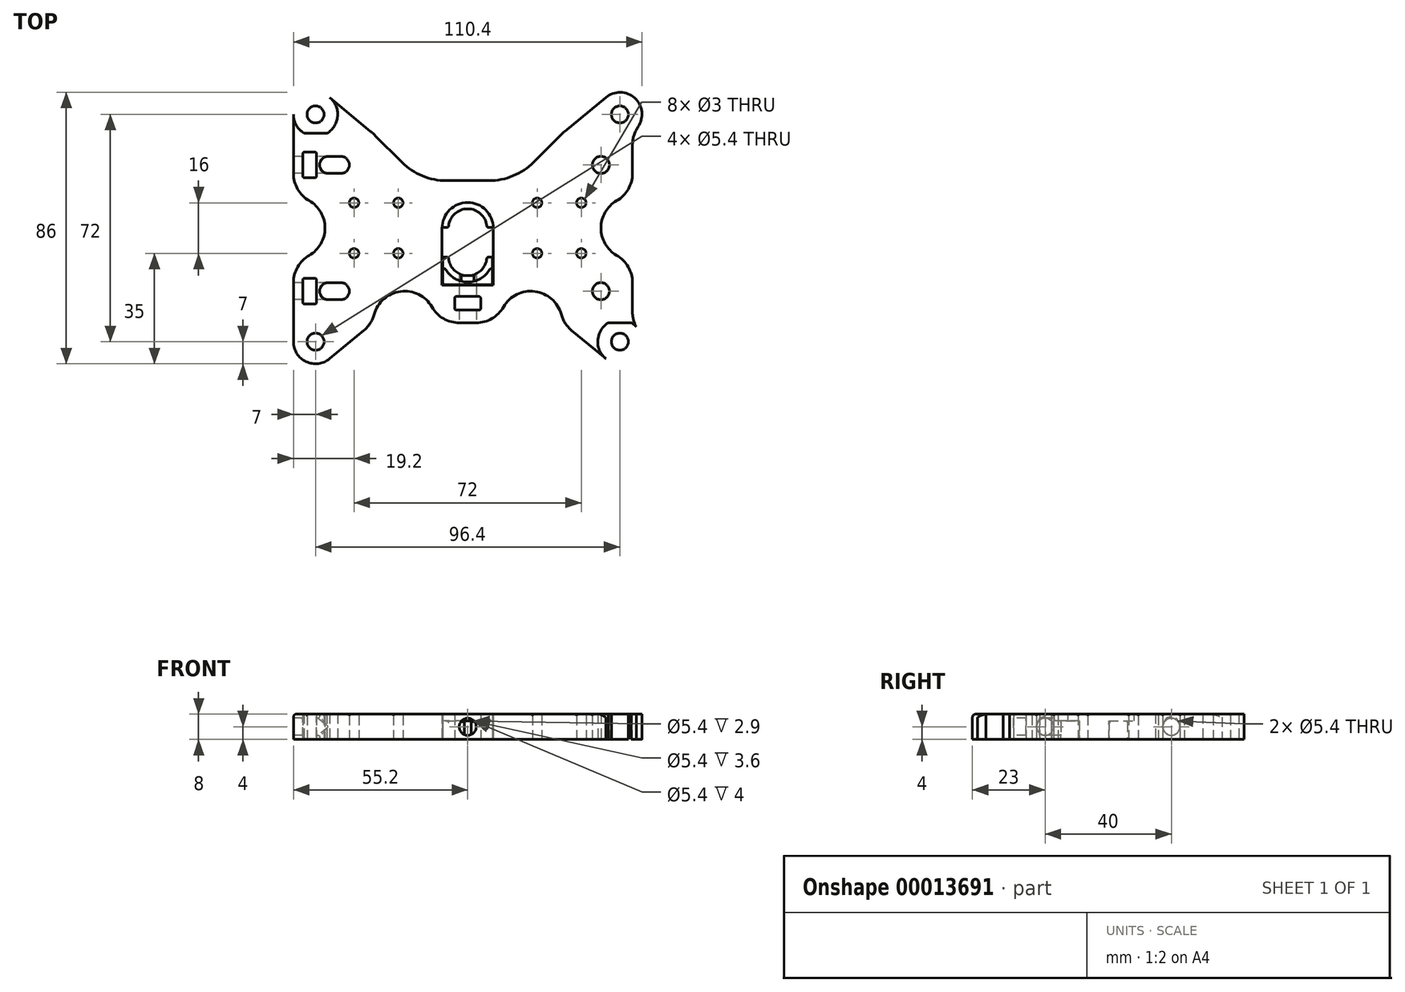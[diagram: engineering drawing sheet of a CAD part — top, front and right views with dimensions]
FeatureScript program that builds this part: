
annotation { "Feature Type Name" : "Feature", "Feature Type Description" : "" }
export const myFeature = defineFeature(function(context is Context, id is Id, definition is map)
    precondition{}
    {
        {
            var Q0;
            Q0=qCreatedBy(makeId("Top.planeOp"),FACE);
            var sketch = newSketch(context, id + "F0", { "sketchPlane" : qUnion([Q0])});
            skLineSegment(sketch, "E0", {"start": v(-12, 175) * mm, "end": v(-12, -175) * mm, "construction": true});
            skLineSegment(sketch, "E1", {"start": v(-32, 175) * mm, "end": v(-32, -175) * mm, "construction": true});
            skLineSegment(sketch, "E2", {"start": v(-32, -175) * mm, "end": v(-12, -175) * mm, "construction": true});
            skLineSegment(sketch, "E3", {"start": v(-32, 175) * mm, "end": v(-12, 175) * mm, "construction": true});
            skLineSegment(sketch, "E4", {"start": v(-12, 0) * mm, "end": v(0, 0) * mm, "construction": true});
            skLineSegment(sketch, "E5", {"start": v(0, 0) * mm, "end": v(0, 158.46) * mm, "construction": true});
            skLineSegment(sketch, "E6.0.MirrorCS", {"start": v(12, 175) * mm, "end": v(12, -175) * mm, "construction": true});
            skLineSegment(sketch, "E7.0.MirrorCS", {"start": v(32, 175) * mm, "end": v(12, 175) * mm, "construction": true});
            skLineSegment(sketch, "E8.0.MirrorCS", {"start": v(32, 175) * mm, "end": v(32, -175) * mm, "construction": true});
            skLineSegment(sketch, "E9.0.MirrorCS", {"start": v(32, -175) * mm, "end": v(12, -175) * mm, "construction": true});
            skLineSegment(sketch, "E10.rect.bottom", {"start": v(42.2, 20) * mm, "end": v(-42.2, 20) * mm, "construction": true});
            skLineSegment(sketch, "E10.rect.top", {"start": v(42.2, -20) * mm, "end": v(-42.2, -20) * mm, "construction": true});
            skLineSegment(sketch, "E10.rect.left", {"start": v(42.2, 20) * mm, "end": v(42.2, -20) * mm, "construction": true});
            skLineSegment(sketch, "E10.rect.right", {"start": v(-42.2, 20) * mm, "end": v(-42.2, -20) * mm, "construction": true});
            skPoint(sketch, "E10.rect.middle", {"position": v(0, 0) * mm});
            skCircle(sketch, "E11", {"center": v(-42.2, 20) * mm, "radius": 12 * mm, "construction": true});
            skCircle(sketch, "E12", {"center": v(42.2, 20) * mm, "radius": 12 * mm, "construction": true});
            skCircle(sketch, "E13", {"center": v(42.2, -20) * mm, "radius": 12 * mm, "construction": true});
            skCircle(sketch, "E14", {"center": v(-42.2, -20) * mm, "radius": 12 * mm, "construction": true});
            skLineSegment(sketch, "E15", {"start": v(-30.2, 175) * mm, "end": v(-30.2, -175) * mm, "construction": true});
            skLineSegment(sketch, "E16", {"start": v(30.2, -175) * mm, "end": v(30.2, 175) * mm, "construction": true});
            skLineSegment(sketch, "E17", {"start": v(-30.2, 0) * mm, "end": v(-32, 0) * mm, "construction": true});
            skLineSegment(sketch, "E18", {"start": v(32, 0) * mm, "end": v(30.2, 0) * mm, "construction": true});
            skArc(sketch, "E19", {"start": v(8.1, 0) * mm, "mid": v(0, 8.1) * mm, "end": v(-8.1, 0) * mm});
            skLineSegment(sketch, "E20.rect.bottom", {"start": v(52.2, 30) * mm, "end": v(-55.2, 30) * mm});
            skLineSegment(sketch, "E20.rect.top", {"start": v(52.2, -30) * mm, "end": v(-55.2, -30) * mm});
            skLineSegment(sketch, "E20.rect.left", {"start": v(52.2, 30) * mm, "end": v(52.2, -30) * mm});
            skLineSegment(sketch, "E20.rect.right", {"start": v(-55.2, 30) * mm, "end": v(-55.2, -30) * mm});
            skCircle(sketch, "E21", {"center": v(42.2, 20) * mm, "radius": 2.7 * mm});
            skCircle(sketch, "E22", {"center": v(42.2, -20) * mm, "radius": 2.7 * mm});
            skArc(sketch, "E23", {"start": v(6.1, 0.2) * mm, "mid": v(0, 6.1) * mm, "end": v(-6.1, 0.2) * mm});
            skCircle(sketch, "E24", {"center": v(0, -6) * mm, "radius": 8.1 * mm, "construction": true});
            skLineSegment(sketch, "E25", {"start": v(-8.1, -9.2) * mm, "end": v(-8.1, -18.1) * mm});
            skLineSegment(sketch, "E26", {"start": v(8.1, -9.2) * mm, "end": v(8.1, -18.1) * mm});
            skLineSegment(sketch, "E27", {"start": v(-8.1, -18.1) * mm, "end": v(8.1, -18.1) * mm});
            skArc(sketch, "E28", {"start": v(-6.1, -9) * mm, "mid": v(0, -15.1) * mm, "end": v(6.1, -9) * mm});
            skLineSegment(sketch, "E29.rect.bottom", {"start": v(4.1, -26) * mm, "end": v(-4.1, -26) * mm});
            skLineSegment(sketch, "E29.rect.top", {"start": v(4.1, -21.7) * mm, "end": v(-4.1, -21.7) * mm});
            skLineSegment(sketch, "E29.rect.left", {"start": v(4.1, -26) * mm, "end": v(4.1, -21.7) * mm});
            skLineSegment(sketch, "E29.rect.right", {"start": v(-4.1, -26) * mm, "end": v(-4.1, -21.7) * mm});
            skPoint(sketch, "E29.rect.middle", {"position": v(0, -23.85) * mm});
            skLineSegment(sketch, "E30", {"start": v(6.1, 0.2) * mm, "end": v(8.1, 0.2) * mm});
            skLineSegment(sketch, "E31", {"start": v(-6.1, 0.2) * mm, "end": v(-8.1, 0.2) * mm});
            skLineSegment(sketch, "E32", {"start": v(6.1, -9.2) * mm, "end": v(8.1, -9.2) * mm});
            skLineSegment(sketch, "E33", {"start": v(-6.1, -9.2) * mm, "end": v(-8.1, -9.2) * mm});
            skLineSegment(sketch, "E34.rect.bottom", {"start": v(-47.9, 24.1) * mm, "end": v(-52.2, 24.1) * mm});
            skLineSegment(sketch, "E34.rect.top", {"start": v(-47.9, 15.9) * mm, "end": v(-52.2, 15.9) * mm});
            skLineSegment(sketch, "E34.rect.left", {"start": v(-47.9, 24.1) * mm, "end": v(-47.9, 15.9) * mm});
            skLineSegment(sketch, "E34.rect.right", {"start": v(-52.2, 24.1) * mm, "end": v(-52.2, 15.9) * mm});
            skPoint(sketch, "E34.rect.middle", {"position": v(-50.05, 20) * mm});
            skLineSegment(sketch, "E35.0.MirrorCS", {"start": v(-47.9, -15.9) * mm, "end": v(-52.2, -15.9) * mm});
            skLineSegment(sketch, "E36.0.MirrorCS", {"start": v(-47.9, -24.1) * mm, "end": v(-47.9, -15.9) * mm});
            skLineSegment(sketch, "E37.0.MirrorCS", {"start": v(-47.9, -24.1) * mm, "end": v(-52.2, -24.1) * mm});
            skLineSegment(sketch, "E38.0.MirrorCS", {"start": v(-52.2, -24.1) * mm, "end": v(-52.2, -15.9) * mm});
            skArc(sketch, "E39", {"start": v(-44.2, 22.7) * mm, "mid": v(-46.9, 20) * mm, "end": v(-44.2, 17.3) * mm});
            skArc(sketch, "E40", {"start": v(-40.2, 17.3) * mm, "mid": v(-37.5, 20) * mm, "end": v(-40.2, 22.7) * mm});
            skLineSegment(sketch, "E41", {"start": v(-40.2, 17.3) * mm, "end": v(-44.2, 17.3) * mm});
            skLineSegment(sketch, "E42", {"start": v(-44.2, 22.7) * mm, "end": v(-40.2, 22.7) * mm});
            skArc(sketch, "E43.0.MirrorCS", {"start": v(-40.2, -17.3) * mm, "mid": v(-37.5, -20) * mm, "end": v(-40.2, -22.7) * mm});
            skLineSegment(sketch, "E44.0.MirrorCS", {"start": v(-44.2, -22.7) * mm, "end": v(-40.2, -22.7) * mm});
            skArc(sketch, "E45.0.MirrorCS", {"start": v(-44.2, -22.7) * mm, "mid": v(-46.9, -20) * mm, "end": v(-44.2, -17.3) * mm});
            skLineSegment(sketch, "E46.0.MirrorCS", {"start": v(-40.2, -17.3) * mm, "end": v(-44.2, -17.3) * mm});
            skLineSegment(sketch, "E47", {"start": v(7.9, -9.2) * mm, "end": v(7.9, -17.9) * mm});
            skLineSegment(sketch, "E48", {"start": v(7.9, -17.9) * mm, "end": v(-7.9, -17.9) * mm});
            skLineSegment(sketch, "E49", {"start": v(-7.9, -17.9) * mm, "end": v(-7.9, -9.2) * mm});
            skLineSegment(sketch, "E50", {"start": v(-30, 30) * mm, "end": v(-15, 15) * mm});
            skLineSegment(sketch, "E51", {"start": v(15, 15) * mm, "end": v(30, 30) * mm});
            skLineSegment(sketch, "E52", {"start": v(15, 15) * mm, "end": v(0, 15) * mm});
            skLineSegment(sketch, "E53", {"start": v(0, 15) * mm, "end": v(-15, 15) * mm});
            skArc(sketch, "E54", {"start": v(-55.2, -10) * mm, "mid": v(-45.2, 0) * mm, "end": v(-55.2, 10) * mm});
            skArc(sketch, "E55", {"start": v(52.2, 10) * mm, "mid": v(42.2, 0) * mm, "end": v(52.2, -10) * mm});
            skArc(sketch, "E56", {"start": v(-10, -30) * mm, "mid": v(-20, -20) * mm, "end": v(-30, -30) * mm});
            skArc(sketch, "E57", {"start": v(30, -30) * mm, "mid": v(20, -20) * mm, "end": v(10, -30) * mm});
            skArc(sketch, "E58", {"start": v(-7.9, -10.79) * mm, "mid": v(0, -17.1) * mm, "end": v(7.9, -10.79) * mm});
            skCircle(sketch, "E59", {"center": v(48.2, 36) * mm, "radius": 2.7 * mm});
            skCircle(sketch, "E60", {"center": v(48.2, 36) * mm, "radius": 7 * mm});
            skCircle(sketch, "E61.0.MirrorC", {"center": v(-48.2, 36) * mm, "radius": 2.7 * mm});
            skCircle(sketch, "E62.0.MirrorC", {"center": v(-48.2, 36) * mm, "radius": 7 * mm});
            skCircle(sketch, "E63.0.MirrorC", {"center": v(48.2, -36) * mm, "radius": 7 * mm});
            skCircle(sketch, "E64.0.MirrorC", {"center": v(48.2, -36) * mm, "radius": 2.7 * mm});
            skCircle(sketch, "E65.0.MirrorC", {"center": v(-48.2, -36) * mm, "radius": 2.7 * mm});
            skCircle(sketch, "E66.0.MirrorC", {"center": v(-48.2, -36) * mm, "radius": 7 * mm});
            skLineSegment(sketch, "E67", {"start": v(43.73, 41.39) * mm, "end": v(30, 30) * mm});
            skLineSegment(sketch, "E68", {"start": v(43.73, -41.39) * mm, "end": v(30, -30) * mm});
            skLineSegment(sketch, "E69", {"start": v(53.37, -31.28) * mm, "end": v(52.2, -30) * mm});
            skLineSegment(sketch, "E70", {"start": v(-43.73, -41.39) * mm, "end": v(-30, -30) * mm});
            skLineSegment(sketch, "E71", {"start": v(-55.2, -36) * mm, "end": v(-55.2, -30) * mm});
            skLineSegment(sketch, "E72", {"start": v(-55.2, 36) * mm, "end": v(-55.2, 30) * mm});
            skLineSegment(sketch, "E73", {"start": v(-43.73, 41.39) * mm, "end": v(-30, 30) * mm});
            skLineSegment(sketch, "E74", {"start": v(53.37, 31.28) * mm, "end": v(52.2, 30) * mm});
            skCircle(sketch, "E75", {"center": v(-22, 8) * mm, "radius": 1.5 * mm});
            skCircle(sketch, "E76.0.MirrorC", {"center": v(22, 8) * mm, "radius": 1.5 * mm});
            skCircle(sketch, "E77.0.MirrorC", {"center": v(22, -8) * mm, "radius": 1.5 * mm});
            skCircle(sketch, "E78.0.MirrorC", {"center": v(-22, -8) * mm, "radius": 1.5 * mm});
            skCircle(sketch, "E79", {"center": v(-36, 8) * mm, "radius": 1.5 * mm});
            skCircle(sketch, "E80.0.MirrorC", {"center": v(36, 8) * mm, "radius": 1.5 * mm});
            skCircle(sketch, "E81.0.MirrorC", {"center": v(-36, -8) * mm, "radius": 1.5 * mm});
            skCircle(sketch, "E82.0.MirrorC", {"center": v(36, -8) * mm, "radius": 1.5 * mm});
            skLineSegment(sketch, "E83", {"start": v(-8.1, -6) * mm, "end": v(-8.1, 0) * mm});
            skLineSegment(sketch, "E84", {"start": v(8.1, -6) * mm, "end": v(8.1, 0) * mm});
            skPoint(sketch, "E85.orphan", {"position": v(6.1, 0) * mm});
            skPoint(sketch, "E86.orphan", {"position": v(-6.1, 0) * mm});
            skLineSegment(sketch, "E87", {"start": v(8.1, -6) * mm, "end": v(8.1, -9.2) * mm});
            skLineSegment(sketch, "E88", {"start": v(-8.1, -6) * mm, "end": v(-8.1, -9.2) * mm});
            skSolve(sketch);
        }
        {
            var Q0;
            Q0=makeQuery(id+"F0.imprint","IMPRINT",FACE,{"disambiguationData":[TD([[makeQuery(id+"F0.imprint","IMPRINT",EDGE,{"derivedFrom":sQuery(id+"F0.wireOp",EDGE,"E21")}),-1.0]])]});
            var Q1;
            {var subQ0=sQuery(id+"F0.wireOp",EDGE,"E67");Q1=makeQuery(id+"F0.imprint","IMPRINT",FACE,{"disambiguationData":[TD([[makeQuery(id+"F0.imprint","IMPRINT",EDGE,{"derivedFrom":subQ0}),1.0]])]});}
            var Q2;
            {var subQ0=sQuery(id+"F0.wireOp",EDGE,"E60");var subQ1=sQuery(id+"F0.wireOp",EDGE,"E20.rect.bottom");var subQ3=makeQuery(id+"F0.imprint","INTERSECT",VERTEX,{"disambiguationData":[OD(0.0)],"derivedFrom":[subQ1,subQ0]});Q2=makeQuery(id+"F0.imprint","IMPRINT",FACE,{"disambiguationData":[TD([[makeQuery(id+"F0.imprint","IMPRINT",EDGE,{"disambiguationData":[TD([[subQ3,-1.0]])],"derivedFrom":subQ1}),1.0]])]});}
            var Q3;
            Q3=makeQuery(id+"F0.imprint","IMPRINT",FACE,{"disambiguationData":[TD([[makeQuery(id+"F0.imprint","IMPRINT",EDGE,{"derivedFrom":sQuery(id+"F0.wireOp",EDGE,"E59")}),-1.0]])]});
            var Q4;
            {var subQ0=sQuery(id+"F0.wireOp",EDGE,"E63.0.MirrorC");var subQ1=sQuery(id+"F0.wireOp",EDGE,"E20.rect.top");var subQ3=makeQuery(id+"F0.imprint","INTERSECT",VERTEX,{"disambiguationData":[OD(0.0)],"derivedFrom":[subQ1,subQ0]});Q4=makeQuery(id+"F0.imprint","IMPRINT",FACE,{"disambiguationData":[TD([[makeQuery(id+"F0.imprint","IMPRINT",EDGE,{"disambiguationData":[TD([[subQ3,-1.0]])],"derivedFrom":subQ1}),-1.0]])]});}
            var Q5;
            {var subQ0=sQuery(id+"F0.wireOp",EDGE,"E68");Q5=makeQuery(id+"F0.imprint","IMPRINT",FACE,{"disambiguationData":[TD([[makeQuery(id+"F0.imprint","IMPRINT",EDGE,{"derivedFrom":subQ0}),-1.0]])]});}
            var Q6;
            Q6=makeQuery(id+"F0.imprint","IMPRINT",FACE,{"disambiguationData":[TD([[makeQuery(id+"F0.imprint","IMPRINT",EDGE,{"derivedFrom":sQuery(id+"F0.wireOp",EDGE,"E64.0.MirrorC")}),1.0]])]});
            var Q7;
            {var subQ0=sQuery(id+"F0.wireOp",EDGE,"E66.0.MirrorC");var subQ1=sQuery(id+"F0.wireOp",EDGE,"E20.rect.top");var subQ3=makeQuery(id+"F0.imprint","INTERSECT",VERTEX,{"disambiguationData":[OD(0.0)],"derivedFrom":[subQ1,subQ0]});Q7=makeQuery(id+"F0.imprint","IMPRINT",FACE,{"disambiguationData":[TD([[makeQuery(id+"F0.imprint","IMPRINT",EDGE,{"disambiguationData":[TD([[subQ3,-1.0]])],"derivedFrom":subQ1}),-1.0]])]});}
            var Q8;
            {var subQ0=sQuery(id+"F0.wireOp",EDGE,"E70");Q8=makeQuery(id+"F0.imprint","IMPRINT",FACE,{"disambiguationData":[TD([[makeQuery(id+"F0.imprint","IMPRINT",EDGE,{"derivedFrom":subQ0}),1.0]])]});}
            var Q9;
            {var subQ0=sQuery(id+"F0.wireOp",EDGE,"E71");Q9=makeQuery(id+"F0.imprint","IMPRINT",FACE,{"disambiguationData":[TD([[makeQuery(id+"F0.imprint","IMPRINT",EDGE,{"derivedFrom":subQ0}),-1.0]])]});}
            var Q10;
            Q10=makeQuery(id+"F0.imprint","IMPRINT",FACE,{"disambiguationData":[TD([[makeQuery(id+"F0.imprint","IMPRINT",EDGE,{"derivedFrom":sQuery(id+"F0.wireOp",EDGE,"E65.0.MirrorC")}),-1.0]])]});
            var Q11;
            {var subQ0=sQuery(id+"F0.wireOp",EDGE,"E72");Q11=makeQuery(id+"F0.imprint","IMPRINT",FACE,{"disambiguationData":[TD([[makeQuery(id+"F0.imprint","IMPRINT",EDGE,{"derivedFrom":subQ0}),1.0]])]});}
            var Q12;
            {var subQ3=sQuery(id+"F0.wireOp",EDGE,"E73");Q12=makeQuery(id+"F0.imprint","IMPRINT",FACE,{"disambiguationData":[TD([[makeQuery(id+"F0.imprint","IMPRINT",EDGE,{"derivedFrom":subQ3}),-1.0]])]});}
            var Q13;
            {var subQ0=sQuery(id+"F0.wireOp",EDGE,"E62.0.MirrorC");var subQ1=sQuery(id+"F0.wireOp",EDGE,"E20.rect.bottom");var subQ3=makeQuery(id+"F0.imprint","INTERSECT",VERTEX,{"disambiguationData":[OD(0.0)],"derivedFrom":[subQ1,subQ0]});Q13=makeQuery(id+"F0.imprint","IMPRINT",FACE,{"disambiguationData":[TD([[makeQuery(id+"F0.imprint","IMPRINT",EDGE,{"disambiguationData":[TD([[subQ3,-1.0]])],"derivedFrom":subQ1}),1.0]])]});}
            var Q14;
            Q14=makeQuery(id+"F0.imprint","IMPRINT",FACE,{"disambiguationData":[TD([[makeQuery(id+"F0.imprint","IMPRINT",EDGE,{"derivedFrom":sQuery(id+"F0.wireOp",EDGE,"E61.0.MirrorC")}),1.0]])]});
            var Q15;
            {var subQ0=sQuery(id+"F0.wireOp",EDGE,"E69");Q15=makeQuery(id+"F0.imprint","IMPRINT",FACE,{"disambiguationData":[TD([[makeQuery(id+"F0.imprint","IMPRINT",EDGE,{"derivedFrom":subQ0}),1.0]])]});}
            var Q16;
            {var subQ0=sQuery(id+"F0.wireOp",EDGE,"E74");Q16=makeQuery(id+"F0.imprint","IMPRINT",FACE,{"disambiguationData":[TD([[makeQuery(id+"F0.imprint","IMPRINT",EDGE,{"derivedFrom":subQ0}),-1.0]])]});}
            extrude(context, id + "F1", {"entities" : qUnion([Q0, Q1, Q2, Q3, Q4, Q5, Q6, Q7, Q8, Q9, Q10, Q11, Q12, Q13, Q14, Q15, Q16]), "depth" : 8 * mm});
        }
        {
            var Q0;
            Q0=makeQuery(id+"F0.imprint","IMPRINT",FACE,{"disambiguationData":[TD([[makeQuery(id+"F0.imprint","IMPRINT",EDGE,{"derivedFrom":sQuery(id+"F0.wireOp",EDGE,"E23")}),-1.0]])]});
            extrude(context, id + "F2", {"entities" : qUnion([Q0]), "operationType" : NewBodyOperationType.ADD, "depth" : 5.8 * mm});
        }
        {
            var Q0;
            {var subQ0=sQuery(id+"F0.wireOp",EDGE,"E58");Q0=makeQuery(id+"F0.imprint","IMPRINT",FACE,{"disambiguationData":[TD([[makeQuery(id+"F0.imprint","IMPRINT",EDGE,{"derivedFrom":subQ0}),1.0]])]});}
            extrude(context, id + "F3", {"entities" : qUnion([Q0]), "depth" : 5.8 * mm});
        }
        {
            var Q0;
            {var subQ2=sQuery(id+"F0.wireOp",EDGE,"E48");Q0=makeQuery(id+"F0.imprint","IMPRINT",FACE,{"disambiguationData":[TD([[makeQuery(id+"F0.imprint","IMPRINT",EDGE,{"derivedFrom":subQ2}),-1.0]])]});}
            extrude(context, id + "F4", {"entities" : qUnion([Q0]), "operationType" : NewBodyOperationType.ADD, "depth" : 8 * mm});
        }
        {
            var Q0;
            {var subQ0=sQuery(id+"F0.wireOp",EDGE,"E20.rect.right");Q0=qUnion([makeQuery(id+"F1.opExtrude","SWEPT_FACE",FACE,{"disambiguationData":[OSD([subQ0,sQuery(id+"F0.wireOp",EDGE,"E72")])]}),makeQuery(id+"F1.opExtrude","SWEPT_FACE",FACE,{"disambiguationData":[OSD([subQ0,sQuery(id+"F0.wireOp",EDGE,"E71")])]})]);}
            var sketch = newSketch(context, id + "F5", { "sketchPlane" : qUnion([Q0])});
            skLineSegment(sketch, "E89.0", {"start": v(-24.1, 8) * mm, "end": v(-15.9, 8) * mm, "construction": true});
            skLineSegment(sketch, "E90.0", {"start": v(24.1, 8) * mm, "end": v(15.9, 8) * mm, "construction": true});
            skLineSegment(sketch, "E91", {"start": v(-20, 8) * mm, "end": v(-20, 4) * mm, "construction": true});
            skCircle(sketch, "E92", {"center": v(-20, 4) * mm, "radius": 2.7 * mm});
            skLineSegment(sketch, "E93", {"start": v(20, 8) * mm, "end": v(20, 4) * mm, "construction": true});
            skCircle(sketch, "E94", {"center": v(20, 4) * mm, "radius": 2.7 * mm});
            skSolve(sketch);
        }
        {
            var Q0;
            Q0=makeQuery(id+"F5.imprint","IMPRINT",FACE,{"disambiguationData":[TD([[makeQuery(id+"F5.imprint","IMPRINT",EDGE,{"derivedFrom":sQuery(id+"F5.wireOp",EDGE,"E92")}),1.0]])]});
            var Q1;
            Q1=makeQuery(id+"F5.imprint","IMPRINT",FACE,{"disambiguationData":[TD([[makeQuery(id+"F5.imprint","IMPRINT",EDGE,{"derivedFrom":sQuery(id+"F5.wireOp",EDGE,"E94")}),1.0]])]});
            extrude(context, id + "F6", {"entities" : qUnion([Q0, Q1]), "operationType" : NewBodyOperationType.REMOVE, "oppositeDirection" : true, "depth" : 12 * mm});
        }
        {
            var Q0;
            Q0=makeQuery(id+"F5.imprint","IMPRINT",FACE,{"disambiguationData":[TD([[makeQuery(id+"F5.imprint","IMPRINT",EDGE,{"derivedFrom":sQuery(id+"F5.wireOp",EDGE,"E92")}),1.0]])]});
            var Q1;
            Q1=makeQuery(id+"F5.imprint","IMPRINT",FACE,{"disambiguationData":[TD([[makeQuery(id+"F5.imprint","IMPRINT",EDGE,{"derivedFrom":sQuery(id+"F5.wireOp",EDGE,"E94")}),1.0]])]});
            extrude(context, id + "F7", {"entities" : qUnion([Q0, Q1]), "operationType" : NewBodyOperationType.REMOVE, "oppositeDirection" : true, "depth" : 12 * mm});
        }
        {
            var Q0;
            Q0=makeQuery(id+"F1.opExtrude","SWEPT_FACE",FACE,{"disambiguationData":[OSD([sQuery(id+"F0.wireOp",EDGE,"E20.rect.top")])]});
            var sketch = newSketch(context, id + "F8", { "sketchPlane" : qUnion([Q0])});
            skLineSegment(sketch, "E95.0", {"start": v(4.1, 8) * mm, "end": v(-4.1, 8) * mm, "construction": true});
            skLineSegment(sketch, "E96", {"start": v(0, 8) * mm, "end": v(0, 4) * mm, "construction": true});
            skCircle(sketch, "E97", {"center": v(0, 4) * mm, "radius": 2.7 * mm});
            skSolve(sketch);
        }
        {
            var Q0;
            Q0=makeQuery(id+"F8.imprint","IMPRINT",FACE,{"disambiguationData":[TD([[makeQuery(id+"F8.imprint","IMPRINT",EDGE,{"derivedFrom":sQuery(id+"F8.wireOp",EDGE,"E97")}),1.0]])]});
            extrude(context, id + "F9", {"entities" : qUnion([Q0]), "operationType" : NewBodyOperationType.REMOVE, "oppositeDirection" : true, "depth" : 15 * mm});
        }
        {
            var Q0;
            {var subQ0=sQuery(id+"F0.wireOp",EDGE,"E20.rect.right");var subQ1=sQuery(id+"F0.wireOp",EDGE,"E54");Q0=makeQuery(id+"F1.opExtrude","SWEPT_EDGE",EDGE,{"disambiguationData":[OSD([subQ0,subQ1]),TDD([makeQuery(id+"F0.imprint","INTERSECT",VERTEX,{"disambiguationData":[OD(0.0)],"derivedFrom":[subQ0,subQ1]})])]});}
            var Q1;
            {var subQ0=sQuery(id+"F0.wireOp",EDGE,"E20.rect.right");var subQ1=sQuery(id+"F0.wireOp",EDGE,"E54");Q1=makeQuery(id+"F1.opExtrude","SWEPT_EDGE",EDGE,{"disambiguationData":[OSD([subQ0,subQ1]),TDD([makeQuery(id+"F0.imprint","INTERSECT",VERTEX,{"disambiguationData":[OD(1.0)],"derivedFrom":[subQ0,subQ1]})])]});}
            var Q2;
            {var subQ0=sQuery(id+"F0.wireOp",EDGE,"E20.rect.left");var subQ1=sQuery(id+"F0.wireOp",EDGE,"E55");Q2=makeQuery(id+"F1.opExtrude","SWEPT_EDGE",EDGE,{"disambiguationData":[OSD([subQ0,subQ1]),TDD([makeQuery(id+"F0.imprint","INTERSECT",VERTEX,{"disambiguationData":[OD(1.0)],"derivedFrom":[subQ0,subQ1]})])]});}
            var Q3;
            {var subQ0=sQuery(id+"F0.wireOp",EDGE,"E20.rect.left");var subQ1=sQuery(id+"F0.wireOp",EDGE,"E55");Q3=makeQuery(id+"F1.opExtrude","SWEPT_EDGE",EDGE,{"disambiguationData":[OSD([subQ0,subQ1]),TDD([makeQuery(id+"F0.imprint","INTERSECT",VERTEX,{"disambiguationData":[OD(0.0)],"derivedFrom":[subQ0,subQ1]})])]});}
            var Q4;
            Q4=makeQuery(id+"F1.opExtrude","SWEPT_EDGE",EDGE,{"disambiguationData":[OSD([sQuery(id+"F0.wireOp",EDGE,"E20.rect.top"),sQuery(id+"F0.wireOp",EDGE,"E57")])]});
            var Q5;
            Q5=makeQuery(id+"F1.opExtrude","SWEPT_EDGE",EDGE,{"disambiguationData":[OSD([sQuery(id+"F0.wireOp",EDGE,"E20.rect.top"),sQuery(id+"F0.wireOp",EDGE,"E57"),sQuery(id+"F0.wireOp",EDGE,"E68")])]});
            var Q6;
            Q6=makeQuery(id+"F1.opExtrude","SWEPT_EDGE",EDGE,{"disambiguationData":[OSD([sQuery(id+"F0.wireOp",EDGE,"E20.rect.top"),sQuery(id+"F0.wireOp",EDGE,"E56")])]});
            var Q7;
            Q7=makeQuery(id+"F1.opExtrude","SWEPT_EDGE",EDGE,{"disambiguationData":[OSD([sQuery(id+"F0.wireOp",EDGE,"E20.rect.top"),sQuery(id+"F0.wireOp",EDGE,"E56"),sQuery(id+"F0.wireOp",EDGE,"E70")])]});
            var Q8;
            Q8=makeQuery(id+"F1.opExtrude","SWEPT_EDGE",EDGE,{"disambiguationData":[OSD([sQuery(id+"F0.wireOp",EDGE,"E20.rect.top"),sQuery(id+"F0.wireOp",EDGE,"E20.rect.left"),sQuery(id+"F0.wireOp",EDGE,"E69")])]});
            var Q9;
            Q9=makeQuery(id+"F1.opExtrude","SWEPT_EDGE",EDGE,{"disambiguationData":[OSD([sQuery(id+"F0.wireOp",EDGE,"E20.rect.bottom"),sQuery(id+"F0.wireOp",EDGE,"E20.rect.left"),sQuery(id+"F0.wireOp",EDGE,"E74")])]});
            fillet(context, id + "F10", {"entities" : qUnion([Q0, Q1, Q2, Q3, Q4, Q5, Q6, Q7, Q8, Q9]), "radius" : 10 * mm, "tangentPropagation" : true, "allowEdgeOverflow" : false});
        }
        {
            var Q0;
            Q0=makeQuery(id+"F1.opExtrude","SWEPT_EDGE",EDGE,{"disambiguationData":[OSD([sQuery(id+"F0.wireOp",EDGE,"E50"),sQuery(id+"F0.wireOp",EDGE,"E53")])]});
            var Q1;
            Q1=makeQuery(id+"F1.opExtrude","SWEPT_EDGE",EDGE,{"disambiguationData":[OSD([sQuery(id+"F0.wireOp",EDGE,"E51"),sQuery(id+"F0.wireOp",EDGE,"E52")])]});
            var Q2;
            Q2=makeQuery(id+"F1.opExtrude","SWEPT_EDGE",EDGE,{"disambiguationData":[OSD([sQuery(id+"F0.wireOp",EDGE,"E20.rect.bottom"),sQuery(id+"F0.wireOp",EDGE,"E51"),sQuery(id+"F0.wireOp",EDGE,"E67")])]});
            var Q3;
            Q3=makeQuery(id+"F1.opExtrude","SWEPT_EDGE",EDGE,{"disambiguationData":[OSD([sQuery(id+"F0.wireOp",EDGE,"E20.rect.bottom"),sQuery(id+"F0.wireOp",EDGE,"E50"),sQuery(id+"F0.wireOp",EDGE,"E73")])]});
            fillet(context, id + "F11", {"entities" : qUnion([Q0, Q1, Q2, Q3]), "radius" : 20 * mm, "tangentPropagation" : true, "allowEdgeOverflow" : false});
        }
        {
            var Q0;
            Q0=makeQuery(id+"F4.opExtrude","SWEPT_EDGE",EDGE,{"disambiguationData":[OSD([sQuery(id+"F0.wireOp",EDGE,"E49"),sQuery(id+"F0.wireOp",EDGE,"E58")])]});
            var Q1;
            Q1=makeQuery(id+"F4.opExtrude","SWEPT_EDGE",EDGE,{"disambiguationData":[OSD([sQuery(id+"F0.wireOp",EDGE,"E47"),sQuery(id+"F0.wireOp",EDGE,"E58")])]});
            var Q2;
            Q2=makeQuery(id+"F3.opExtrude","SWEPT_EDGE",EDGE,{"disambiguationData":[OSD([sQuery(id+"F0.wireOp",EDGE,"E28"),sQuery(id+"F0.wireOp",EDGE,"E33")])]});
            var Q3;
            Q3=makeQuery(id+"F3.opExtrude","SWEPT_EDGE",EDGE,{"disambiguationData":[OSD([sQuery(id+"F0.wireOp",EDGE,"E28"),sQuery(id+"F0.wireOp",EDGE,"E32")])]});
            var Q4;
            Q4=makeQuery(id+"F3.opExtrude","SWEPT_EDGE",EDGE,{"disambiguationData":[OSD([sQuery(id+"F0.wireOp",EDGE,"E32"),sQuery(id+"F0.wireOp",EDGE,"E47")])]});
            var Q5;
            Q5=makeQuery(id+"F3.opExtrude","SWEPT_EDGE",EDGE,{"disambiguationData":[OSD([sQuery(id+"F0.wireOp",EDGE,"E33"),sQuery(id+"F0.wireOp",EDGE,"E49")])]});
            var Q6;
            Q6=makeQuery(id+"F4.opExtrude","SWEPT_EDGE",EDGE,{"disambiguationData":[OSD([sQuery(id+"F0.wireOp",EDGE,"E48"),sQuery(id+"F0.wireOp",EDGE,"E49")])]});
            var Q7;
            Q7=makeQuery(id+"F4.opExtrude","SWEPT_EDGE",EDGE,{"disambiguationData":[OSD([sQuery(id+"F0.wireOp",EDGE,"E47"),sQuery(id+"F0.wireOp",EDGE,"E48")])]});
            var Q8;
            Q8=makeQuery(id+"F3.opExtrude","CAP_EDGE",EDGE,{"disambiguationData":[OSD([sQuery(id+"F0.wireOp",EDGE,"E28")])],"isStart":false});
            fillet(context, id + "F12", {"entities" : qUnion([Q0, Q1, Q2, Q3, Q4, Q5, Q6, Q7, Q8]), "radius" : 0.5 * mm, "tangentPropagation" : true, "allowEdgeOverflow" : false});
        }
        {
            var Q0;
            Q0=makeQuery(id+"F2.opExtrude","SWEPT_EDGE",EDGE,{"disambiguationData":[OSD([sQuery(id+"F0.wireOp",EDGE,"E23"),sQuery(id+"F0.wireOp",EDGE,"E31")])]});
            var Q1;
            Q1=makeQuery(id+"F2.opExtrude","SWEPT_EDGE",EDGE,{"disambiguationData":[OSD([sQuery(id+"F0.wireOp",EDGE,"E23"),sQuery(id+"F0.wireOp",EDGE,"E30")])]});
            var Q2;
            Q2=makeQuery(id+"F2.opExtrude","CAP_EDGE",EDGE,{"disambiguationData":[OSD([sQuery(id+"F0.wireOp",EDGE,"E23")])],"isStart":false});
            fillet(context, id + "F13", {"entities" : qUnion([Q0, Q1, Q2]), "radius" : 0.5 * mm, "tangentPropagation" : true, "allowEdgeOverflow" : false});
        }
        {
            var Q0;
            Q0=makeQuery(id+"F1.opExtrude","SWEPT_EDGE",EDGE,{"disambiguationData":[OSD([sQuery(id+"F0.wireOp",EDGE,"E29.rect.top"),sQuery(id+"F0.wireOp",EDGE,"E29.rect.right")])]});
            var Q1;
            Q1=makeQuery(id+"F1.opExtrude","SWEPT_EDGE",EDGE,{"disambiguationData":[OSD([sQuery(id+"F0.wireOp",EDGE,"E29.rect.top"),sQuery(id+"F0.wireOp",EDGE,"E29.rect.left")])]});
            var Q2;
            Q2=makeQuery(id+"F1.opExtrude","SWEPT_EDGE",EDGE,{"disambiguationData":[OSD([sQuery(id+"F0.wireOp",EDGE,"E29.rect.bottom"),sQuery(id+"F0.wireOp",EDGE,"E29.rect.left")])]});
            var Q3;
            Q3=makeQuery(id+"F1.opExtrude","SWEPT_EDGE",EDGE,{"disambiguationData":[OSD([sQuery(id+"F0.wireOp",EDGE,"E29.rect.bottom"),sQuery(id+"F0.wireOp",EDGE,"E29.rect.right")])]});
            var Q4;
            Q4=makeQuery(id+"F1.opExtrude","SWEPT_EDGE",EDGE,{"disambiguationData":[OSD([sQuery(id+"F0.wireOp",EDGE,"E35.0.MirrorCS"),sQuery(id+"F0.wireOp",EDGE,"E36.0.MirrorCS")])]});
            var Q5;
            Q5=makeQuery(id+"F1.opExtrude","SWEPT_EDGE",EDGE,{"disambiguationData":[OSD([sQuery(id+"F0.wireOp",EDGE,"E36.0.MirrorCS"),sQuery(id+"F0.wireOp",EDGE,"E37.0.MirrorCS")])]});
            var Q6;
            Q6=makeQuery(id+"F1.opExtrude","SWEPT_EDGE",EDGE,{"disambiguationData":[OSD([sQuery(id+"F0.wireOp",EDGE,"E37.0.MirrorCS"),sQuery(id+"F0.wireOp",EDGE,"E38.0.MirrorCS")])]});
            var Q7;
            Q7=makeQuery(id+"F1.opExtrude","SWEPT_EDGE",EDGE,{"disambiguationData":[OSD([sQuery(id+"F0.wireOp",EDGE,"E35.0.MirrorCS"),sQuery(id+"F0.wireOp",EDGE,"E38.0.MirrorCS")])]});
            var Q8;
            Q8=makeQuery(id+"F1.opExtrude","SWEPT_EDGE",EDGE,{"disambiguationData":[OSD([sQuery(id+"F0.wireOp",EDGE,"E34.rect.top"),sQuery(id+"F0.wireOp",EDGE,"E34.rect.left")])]});
            var Q9;
            Q9=makeQuery(id+"F1.opExtrude","SWEPT_EDGE",EDGE,{"disambiguationData":[OSD([sQuery(id+"F0.wireOp",EDGE,"E34.rect.top"),sQuery(id+"F0.wireOp",EDGE,"E34.rect.right")])]});
            var Q10;
            Q10=makeQuery(id+"F1.opExtrude","SWEPT_EDGE",EDGE,{"disambiguationData":[OSD([sQuery(id+"F0.wireOp",EDGE,"E34.rect.bottom"),sQuery(id+"F0.wireOp",EDGE,"E34.rect.right")])]});
            var Q11;
            Q11=makeQuery(id+"F1.opExtrude","SWEPT_EDGE",EDGE,{"disambiguationData":[OSD([sQuery(id+"F0.wireOp",EDGE,"E34.rect.bottom"),sQuery(id+"F0.wireOp",EDGE,"E34.rect.left")])]});
            fillet(context, id + "F14", {"entities" : qUnion([Q0, Q1, Q2, Q3, Q4, Q5, Q6, Q7, Q8, Q9, Q10, Q11]), "radius" : 0.5 * mm, "tangentPropagation" : true, "allowEdgeOverflow" : false});
        }
        {
            var Q0;
            Q0=makeQuery(id+"F1.opExtrude","CAP_EDGE",EDGE,{"disambiguationData":[OSD([sQuery(id+"F0.wireOp",EDGE,"E64.0.MirrorC")])],"isStart":false});
            var Q1;
            Q1=makeQuery(id+"F1.opExtrude","CAP_EDGE",EDGE,{"disambiguationData":[OSD([sQuery(id+"F0.wireOp",EDGE,"E22")])],"isStart":false});
            var Q2;
            Q2=makeQuery(id+"F1.opExtrude","CAP_EDGE",EDGE,{"disambiguationData":[OSD([sQuery(id+"F0.wireOp",EDGE,"E21")])],"isStart":false});
            var Q3;
            Q3=makeQuery(id+"F1.opExtrude","CAP_EDGE",EDGE,{"disambiguationData":[OSD([sQuery(id+"F0.wireOp",EDGE,"E59")])],"isStart":false});
            var Q4;
            Q4=makeQuery(id+"F1.opExtrude","CAP_EDGE",EDGE,{"disambiguationData":[OSD([sQuery(id+"F0.wireOp",EDGE,"E61.0.MirrorC")])],"isStart":false});
            var Q5;
            Q5=makeQuery(id+"F1.opExtrude","CAP_EDGE",EDGE,{"disambiguationData":[OSD([sQuery(id+"F0.wireOp",EDGE,"E40")])],"isStart":false});
            var Q6;
            Q6=makeQuery(id+"F1.opExtrude","CAP_EDGE",EDGE,{"disambiguationData":[OSD([sQuery(id+"F0.wireOp",EDGE,"E43.0.MirrorCS")])],"isStart":false});
            var Q7;
            Q7=makeQuery(id+"F1.opExtrude","CAP_EDGE",EDGE,{"disambiguationData":[OSD([sQuery(id+"F0.wireOp",EDGE,"E65.0.MirrorC")])],"isStart":false});
            var Q8;
            Q8=makeQuery(id+"F1.opExtrude","CAP_EDGE",EDGE,{"disambiguationData":[OSD([sQuery(id+"F0.wireOp",EDGE,"E35.0.MirrorCS")])],"isStart":false});
            var Q9;
            Q9=makeQuery(id+"F1.opExtrude","CAP_EDGE",EDGE,{"disambiguationData":[OSD([sQuery(id+"F0.wireOp",EDGE,"E34.rect.top")])],"isStart":false});
            var Q10;
            Q10=makeQuery(id+"F1.opExtrude","CAP_EDGE",EDGE,{"disambiguationData":[OSD([sQuery(id+"F0.wireOp",EDGE,"E29.rect.top")])],"isStart":false});
            var Q11;
            Q11=makeQuery(id+"F1.opExtrude","CAP_EDGE",EDGE,{"disambiguationData":[OSD([sQuery(id+"F0.wireOp",EDGE,"E77.0.MirrorC")])],"isStart":false});
            var Q12;
            Q12=makeQuery(id+"F1.opExtrude","CAP_EDGE",EDGE,{"disambiguationData":[OSD([sQuery(id+"F0.wireOp",EDGE,"E76.0.MirrorC")])],"isStart":false});
            var Q13;
            Q13=makeQuery(id+"F1.opExtrude","CAP_EDGE",EDGE,{"disambiguationData":[OSD([sQuery(id+"F0.wireOp",EDGE,"E80.0.MirrorC")])],"isStart":false});
            var Q14;
            Q14=makeQuery(id+"F1.opExtrude","CAP_EDGE",EDGE,{"disambiguationData":[OSD([sQuery(id+"F0.wireOp",EDGE,"E82.0.MirrorC")])],"isStart":false});
            var Q15;
            Q15=makeQuery(id+"F1.opExtrude","CAP_EDGE",EDGE,{"disambiguationData":[OSD([sQuery(id+"F0.wireOp",EDGE,"E78.0.MirrorC")])],"isStart":false});
            var Q16;
            Q16=makeQuery(id+"F1.opExtrude","CAP_EDGE",EDGE,{"disambiguationData":[OSD([sQuery(id+"F0.wireOp",EDGE,"E75")])],"isStart":false});
            var Q17;
            Q17=makeQuery(id+"F1.opExtrude","CAP_EDGE",EDGE,{"disambiguationData":[OSD([sQuery(id+"F0.wireOp",EDGE,"E81.0.MirrorC")])],"isStart":false});
            var Q18;
            Q18=makeQuery(id+"F1.opExtrude","CAP_EDGE",EDGE,{"disambiguationData":[OSD([sQuery(id+"F0.wireOp",EDGE,"E79")])],"isStart":false});
            fillet(context, id + "F15", {"entities" : qUnion([Q0, Q1, Q2, Q3, Q4, Q5, Q6, Q7, Q8, Q9, Q10, Q11, Q12, Q13, Q14, Q15, Q16, Q17, Q18]), "radius" : 0.5 * mm, "tangentPropagation" : true, "allowEdgeOverflow" : false});
        }
        {
            var Q0;
            Q0=makeQuery(id+"F1.opExtrude","CAP_EDGE",EDGE,{"disambiguationData":[OSD([sQuery(id+"F0.wireOp",EDGE,"E57")])],"isStart":false});
            fillet(context, id + "F16", {"entities" : qUnion([Q0]), "radius" : 1 * mm, "tangentPropagation" : true, "allowEdgeOverflow" : false});
        }
        {
            var Q0;
            {var subQ0=makeQuery(id+"F9.boolean.opBoolean","COPY",EDGE,{"derivedFrom":makeQuery(id+"F9.opExtrude","CAP_EDGE",EDGE,{"disambiguationData":[OSD([sQuery(id+"F8.wireOp",EDGE,"E97")])],"isStart":true})});Q0=qUnion([subQ0,subQ0]);}
            var Q1;
            Q1=makeQuery(id+"F6.boolean.opBoolean","COPY",EDGE,{"derivedFrom":makeQuery(id+"F6.opExtrude","CAP_EDGE",EDGE,{"disambiguationData":[OSD([sQuery(id+"F5.wireOp",EDGE,"E94")])],"isStart":true})});
            var Q2;
            Q2=makeQuery(id+"F6.boolean.opBoolean","COPY",EDGE,{"derivedFrom":makeQuery(id+"F6.opExtrude","CAP_EDGE",EDGE,{"disambiguationData":[OSD([sQuery(id+"F5.wireOp",EDGE,"E92")])],"isStart":true})});
            var Q3;
            Q3=makeQuery(id+"F6.boolean.opBoolean","INTERSECT",EDGE,{"derivedFrom":[makeQuery(id+"F1.opExtrude","SWEPT_FACE",FACE,{"disambiguationData":[OSD([sQuery(id+"F0.wireOp",EDGE,"E34.rect.right")])]}),makeQuery(id+"F6.opExtrude","SWEPT_FACE",FACE,{"disambiguationData":[OSD([sQuery(id+"F5.wireOp",EDGE,"E92")])]})]});
            var Q4;
            Q4=makeQuery(id+"F6.boolean.opBoolean","INTERSECT",EDGE,{"derivedFrom":[makeQuery(id+"F1.opExtrude","SWEPT_FACE",FACE,{"disambiguationData":[OSD([sQuery(id+"F0.wireOp",EDGE,"E34.rect.left")])]}),makeQuery(id+"F6.opExtrude","SWEPT_FACE",FACE,{"disambiguationData":[OSD([sQuery(id+"F5.wireOp",EDGE,"E92")])]})]});
            var Q5;
            Q5=makeQuery(id+"F6.boolean.opBoolean","INTERSECT",EDGE,{"disambiguationData":[OD(1.0)],"derivedFrom":[makeQuery(id+"F1.opExtrude","SWEPT_FACE",FACE,{"disambiguationData":[OSD([sQuery(id+"F0.wireOp",EDGE,"E39")])]}),makeQuery(id+"F6.opExtrude","SWEPT_FACE",FACE,{"disambiguationData":[OSD([sQuery(id+"F5.wireOp",EDGE,"E92")])]})]});
            var Q6;
            Q6=makeQuery(id+"F6.boolean.opBoolean","INTERSECT",EDGE,{"disambiguationData":[OD(0.0)],"derivedFrom":[makeQuery(id+"F1.opExtrude","SWEPT_FACE",FACE,{"disambiguationData":[OSD([sQuery(id+"F0.wireOp",EDGE,"E39")])]}),makeQuery(id+"F6.opExtrude","SWEPT_FACE",FACE,{"disambiguationData":[OSD([sQuery(id+"F5.wireOp",EDGE,"E92")])]})]});
            var Q7;
            Q7=makeQuery(id+"F6.boolean.opBoolean","INTERSECT",EDGE,{"derivedFrom":[makeQuery(id+"F1.opExtrude","SWEPT_FACE",FACE,{"disambiguationData":[OSD([sQuery(id+"F0.wireOp",EDGE,"E38.0.MirrorCS")])]}),makeQuery(id+"F6.opExtrude","SWEPT_FACE",FACE,{"disambiguationData":[OSD([sQuery(id+"F5.wireOp",EDGE,"E94")])]})]});
            var Q8;
            Q8=makeQuery(id+"F6.boolean.opBoolean","INTERSECT",EDGE,{"derivedFrom":[makeQuery(id+"F1.opExtrude","SWEPT_FACE",FACE,{"disambiguationData":[OSD([sQuery(id+"F0.wireOp",EDGE,"E36.0.MirrorCS")])]}),makeQuery(id+"F6.opExtrude","SWEPT_FACE",FACE,{"disambiguationData":[OSD([sQuery(id+"F5.wireOp",EDGE,"E94")])]})]});
            var Q9;
            Q9=makeQuery(id+"F6.boolean.opBoolean","INTERSECT",EDGE,{"disambiguationData":[OD(0.0)],"derivedFrom":[makeQuery(id+"F1.opExtrude","SWEPT_FACE",FACE,{"disambiguationData":[OSD([sQuery(id+"F0.wireOp",EDGE,"E45.0.MirrorCS")])]}),makeQuery(id+"F6.opExtrude","SWEPT_FACE",FACE,{"disambiguationData":[OSD([sQuery(id+"F5.wireOp",EDGE,"E94")])]})]});
            var Q10;
            Q10=makeQuery(id+"F6.boolean.opBoolean","INTERSECT",EDGE,{"disambiguationData":[OD(1.0)],"derivedFrom":[makeQuery(id+"F1.opExtrude","SWEPT_FACE",FACE,{"disambiguationData":[OSD([sQuery(id+"F0.wireOp",EDGE,"E45.0.MirrorCS")])]}),makeQuery(id+"F6.opExtrude","SWEPT_FACE",FACE,{"disambiguationData":[OSD([sQuery(id+"F5.wireOp",EDGE,"E94")])]})]});
            fillet(context, id + "F17", {"entities" : qUnion([Q0, Q1, Q2, Q3, Q4, Q5, Q6, Q7, Q8, Q9, Q10]), "radius" : 0.5 * mm, "tangentPropagation" : true, "allowEdgeOverflow" : false});
        }
    });
